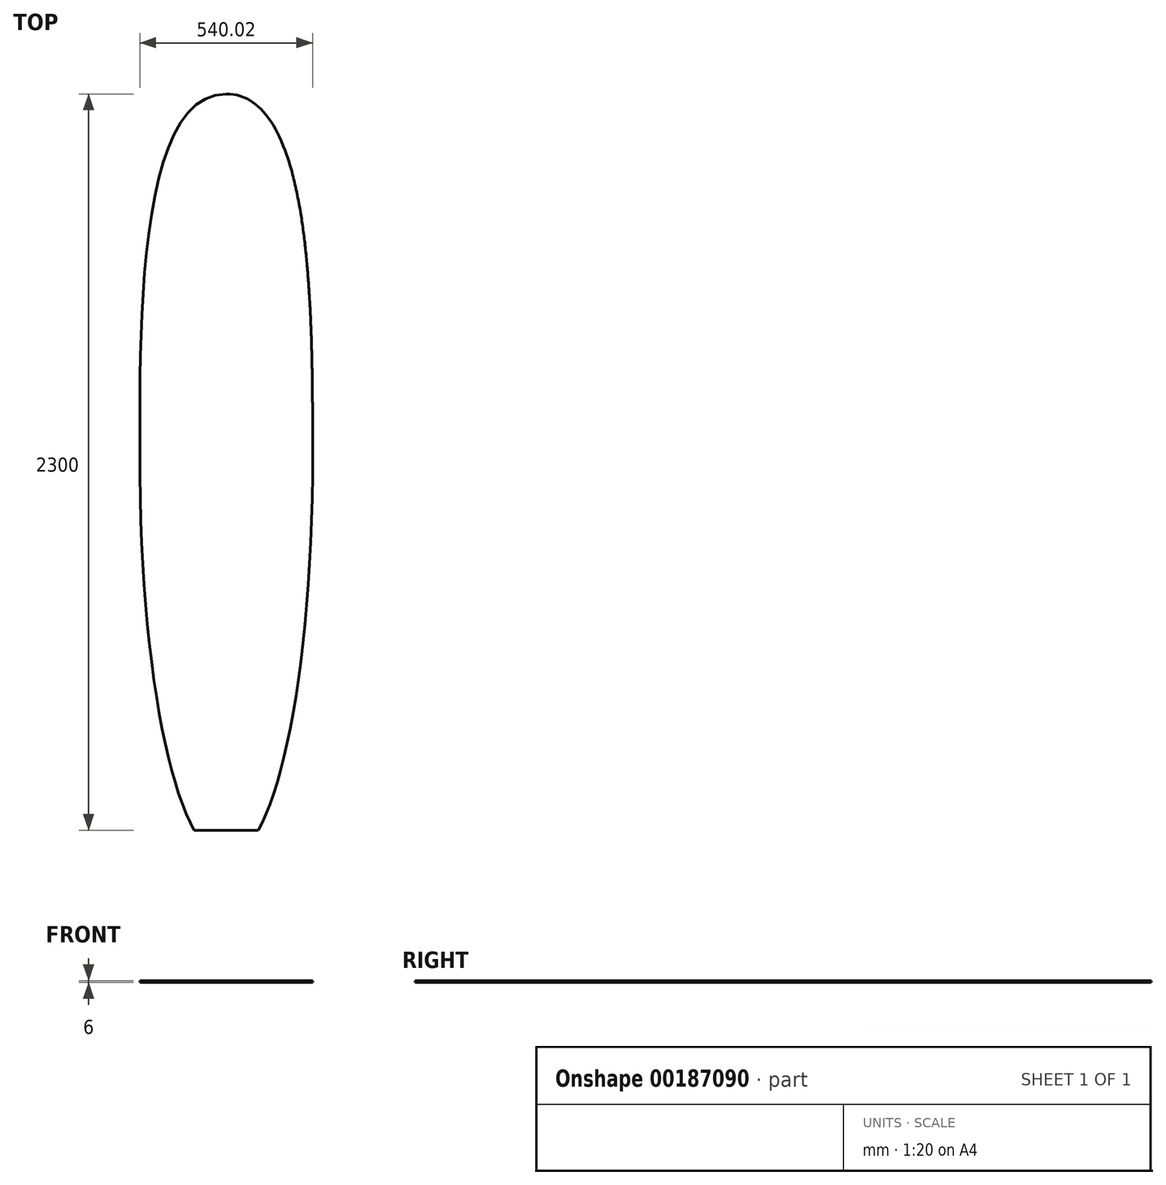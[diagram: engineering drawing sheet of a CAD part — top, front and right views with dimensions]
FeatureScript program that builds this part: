
annotation { "Feature Type Name" : "Feature", "Feature Type Description" : "" }
export const myFeature = defineFeature(function(context is Context, id is Id, definition is map)
    precondition{}
    {
        {
            var Q0;
            Q0=qCreatedBy(makeId("Front.planeOp"),FACE);
            var sketch = newSketch(context, id + "F0", { "sketchPlane" : qUnion([Q0])});
            skLineSegment(sketch, "E0.bottom", {"start": v(0, 0) * mm, "end": v(260, 0) * mm});
            skLineSegment(sketch, "E0.top", {"start": v(0, 73) * mm, "end": v(260, 73) * mm});
            skLineSegment(sketch, "E0.left", {"start": v(0, 0) * mm, "end": v(0, 73) * mm});
            skLineSegment(sketch, "E0.right", {"start": v(260, 0) * mm, "end": v(260, 73) * mm});
            skLineSegment(sketch, "E1", {"start": v(248, 0) * mm, "end": v(248, 73) * mm, "construction": true});
            skLineSegment(sketch, "E2", {"start": v(248, 40) * mm, "end": v(38, 73) * mm, "construction": true});
            skArc(sketch, "E3", {"start": v(248, 40) * mm, "mid": v(125.1, 64.71) * mm, "end": v(0, 73) * mm});
            skLineSegment(sketch, "E4", {"start": v(102, 0) * mm, "end": v(248, 8) * mm, "construction": true});
            skArc(sketch, "E5", {"start": v(102, 0) * mm, "mid": v(175.1, 2) * mm, "end": v(248, 8) * mm});
            skLineSegment(sketch, "E6", {"start": v(248, 24) * mm, "end": v(260, 24) * mm, "construction": true});
            skFitSpline(sketch, "E7", {"points": [v(260, 24) * mm, v(248, 40) * mm], "startDerivative": vector(0, 26.32) * mm, "endDerivative": vector(-24.23, 6.56) * mm});
            skFitSpline(sketch, "E8", {"points": [v(248, 8) * mm, v(260, 24) * mm], "startDerivative": vector(24.95, 2.74) * mm, "endDerivative": vector(0, 25.1) * mm});
            skLineSegment(sketch, "E9", {"start": v(248, 8) * mm, "end": v(275.27, 11) * mm});
            skLineSegment(sketch, "E10", {"start": v(260, 24) * mm, "end": v(261.63, 9.14) * mm});
            skPoint(sketch, "E10.endSnap0", {"position": v(261.63, 9.5) * mm});
            skArc(sketch, "E11.0", {"start": v(102, 3) * mm, "mid": v(174.95, 5) * mm, "end": v(247.67, 10.98) * mm});
            skLineSegment(sketch, "E12.0", {"start": v(247.67, 10.98) * mm, "end": v(274.94, 13.98) * mm});
            skLineSegment(sketch, "E13", {"start": v(260.61, 18.44) * mm, "end": v(254.65, 17.78) * mm});
            skLineSegment(sketch, "E14", {"start": v(254.65, 17.78) * mm, "end": v(255.3, 11.82) * mm});
            skLineSegment(sketch, "E15", {"start": v(126.2, 73) * mm, "end": v(260, 36.75) * mm, "construction": true});
            skSolve(sketch);
        }
        {
            var Q0;
            Q0=qCreatedBy(makeId("Top.planeOp"),FACE);
            var sketch = newSketch(context, id + "F1", { "sketchPlane" : qUnion([Q0])});
            skLineSegment(sketch, "E16", {"start": v(424.79, 0) * mm, "end": v(0, 0) * mm, "construction": true});
            skLineSegment(sketch, "E17", {"start": v(0, 0) * mm, "end": v(0, 2300) * mm, "construction": true});
            skLineSegment(sketch, "E18", {"start": v(0, 2300) * mm, "end": v(166.4, 2300) * mm, "construction": true});
            skLineSegment(sketch, "E19", {"start": v(270, 1497.86) * mm, "end": v(270, 768.16) * mm, "construction": true});
            skLineSegment(sketch, "E20", {"start": v(0, 1180) * mm, "end": v(270, 1180) * mm, "construction": true});
            skLineSegment(sketch, "E21", {"start": v(0, 0) * mm, "end": v(100, 0) * mm});
            skFitSpline(sketch, "E22", {"points": [v(0, 2300) * mm, v(270, 1180) * mm], "startDerivative": vector(821.37, 0) * mm, "endDerivative": vector(0, -1243.68) * mm});
            skFitSpline(sketch, "E23", {"points": [v(270, 1180) * mm, v(100, 0) * mm], "startDerivative": vector(3.29, -1680.26) * mm, "endDerivative": vector(-291.25, -512.73) * mm});
            skLineSegment(sketch, "E24.MirrorCS", {"start": v(0, 0) * mm, "end": v(-100, 0) * mm});
            skFitSpline(sketch, "E25.MirrorCS", {"points": [v(-270, 1180) * mm, v(-100, 0) * mm], "startDerivative": vector(-3.29, -1680.26) * mm, "endDerivative": vector(291.25, -512.73) * mm});
            skFitSpline(sketch, "E26.MirrorCS", {"points": [v(0, 2300) * mm, v(-270, 1180) * mm], "startDerivative": vector(-821.37, 0) * mm, "endDerivative": vector(0, -1243.68) * mm});
            skLineSegment(sketch, "E27", {"start": v(270, 1180) * mm, "end": v(20, 1430) * mm});
            skLineSegment(sketch, "E28", {"start": v(0, 1591.42) * mm, "end": v(269.79, 1321.63) * mm});
            skLineSegment(sketch, "E29.0.1.0", {"start": v(270, 1321.42) * mm, "end": v(0, 1591.42) * mm});
            skLineSegment(sketch, "E29.0.2.0", {"start": v(270, 1462.84) * mm, "end": v(0, 1732.84) * mm});
            skLineSegment(sketch, "E29.0.3.0", {"start": v(263.13, 1611.14) * mm, "end": v(0, 1874.26) * mm});
            skLineSegment(sketch, "E29.0.4.0", {"start": v(253, 1762.7) * mm, "end": v(20, 1995.68) * mm});
            skLineSegment(sketch, "E29.0.5.0", {"start": v(233.32, 1923.79) * mm, "end": v(0, 2157.1) * mm});
            skLineSegment(sketch, "E29.0.6.0", {"start": v(270, 2028.53) * mm, "end": v(0, 2298.53) * mm});
            skLineSegment(sketch, "E29.0.7.0", {"start": v(270, 2169.95) * mm, "end": v(0, 2439.95) * mm});
            skLineSegment(sketch, "E29.0.8.0", {"start": v(270, 2311.37) * mm, "end": v(0, 2581.37) * mm});
            skLineSegment(sketch, "E29.0.9.0", {"start": v(270, 2452.79) * mm, "end": v(0, 2722.79) * mm});
            skLineSegment(sketch, "E29.0.10.0", {"start": v(270, 2594.2) * mm, "end": v(0, 2864.2) * mm});
            skLineSegment(sketch, "E29.0.11.0", {"start": v(270, 2735.63) * mm, "end": v(0, 3005.63) * mm});
            skLineSegment(sketch, "E29.0.12.0", {"start": v(270, 2877.05) * mm, "end": v(0, 3147.05) * mm});
            skLineSegment(sketch, "E29.0.13.0", {"start": v(270, 3018.47) * mm, "end": v(0, 3288.47) * mm});
            skLineSegment(sketch, "E29.0.14.0", {"start": v(270, 3159.9) * mm, "end": v(0, 3429.9) * mm});
            skLineSegment(sketch, "E29.direction1", {"start": v(270, 1180) * mm, "end": v(295, 1180) * mm, "construction": true});
            skLineSegment(sketch, "E29.direction2", {"start": v(270, 1180) * mm, "end": v(270, 1321.42) * mm, "construction": true});
            skPoint(sketch, "E30.orphan", {"position": v(270, 1745.68) * mm});
            skPoint(sketch, "E31.orphan", {"position": v(270, 1604.26) * mm});
            skPoint(sketch, "E32.orphan", {"position": v(270, 1887.1) * mm});
            skLineSegment(sketch, "E33.1.0.0", {"start": v(20, 0) * mm, "end": v(20, 2300) * mm, "construction": true});
            skLineSegment(sketch, "E33.direction1", {"start": v(0, 0) * mm, "end": v(20, 0) * mm, "construction": true});
            skPoint(sketch, "E34.orphan", {"position": v(0, 1450) * mm});
            skPoint(sketch, "E35.orphan", {"position": v(0, 2015.68) * mm});
            skSolve(sketch);
        }
        {
            var Q0;
            Q0 = qSketchRegion(id + "F1", true);
            extrude(context, id + "F2", {"entities" : qUnion([Q0]), "depth" : 6 * mm});
        }
    });
